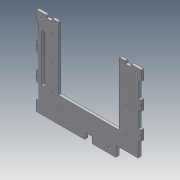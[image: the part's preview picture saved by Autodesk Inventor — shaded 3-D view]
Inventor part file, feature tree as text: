
AUTODESK INVENTOR PART (.ipt)
format: ipt  version: 2014 (Build 180170000, 170)  size: 314,368 bytes
history: native  units: mm
features: extrude x9, sketch x9, fillet x2
ambient origin geometry x8: Origin, YZ Plane, XZ Plane, XY Plane, X Axis, Y Axis, Z Axis, Center Point
bodies: Solid1 (feature_tree)
feature tree (20):
  extrude  "Extrusion1"  Depth=175.0mm
  extrude  "Extrusion2"  Depth=185.0mm
  extrude  "Extrusion3"  Depth=6.0mm TaperAngle=0.0deg
  extrude  "Extrusion4"  Depth=59.0mm
  extrude  "Extrusion5"  Depth=6.0mm TaperAngle=0.0deg
  extrude  "Extrusion6"  Depth=8.0mm
  extrude  "Extrusion7"  Depth=108.0mm
  extrude  "Extrusion8"  Depth=60.0mm
  extrude  "Extrusion9"  Depth=175.0mm
  fillet  "Fillet1"  Radius=3.2mm
  fillet  "Fillet2"  Radius=150.0mm
  sketch  "Sketch1"  dims[d0=175.0mm d1=87.5mm]
  sketch  "Sketch2"  dims[d2=145.0mm d4=185.0mm]
  sketch  "Sketch3"  dims[d5=250.0mm d6=6.0mm d7=0.0mm]
  sketch  "Sketch4"  dims[d8=3.0mm d9=0.0mm d10=59.0mm]
  sketch  "Sketch5"  dims[d11=25.0mm d13=6.0mm d14=0.0mm]
  sketch  "Sketch6"  dims[d15=35.0mm d16=8.0mm]
  sketch  "Sketch7"  dims[d17=108.0mm d18=40.0mm]
  sketch  "Sketch8"  dims[d19=10.0mm d20=0.0mm d21=60.0mm]
  sketch  "Sketch9"  dims[d22=60.0mm d23=175.0mm d24=3.2mm d25=150.0mm d26=15.0mm d27=10.0mm d28=0.0mm d29=50.0mm d30=54.0mm d31=3.0mm d32=4.4mm d33=30.0mm d34=15.0mm d35=10.0mm d36=0.0mm d37=2.0mm d38=16.0mm d39=15.0mm d40=10.0mm d41=0.0mm d42=12.5mm d43=50.0mm d44=50.0mm d45=5.4mm d46=12.5mm d47=12.5mm d48=12.5mm d49=5.4mm d50=25.0mm d51=6.1mm d52=25.0mm d53=25.0mm d54=2.2mm d55=12.5mm d56=12.5mm d57=10.0mm d58=0.0mm d59=2.0mm d60=12.5mm d63=10.0mm d64=0.0mm d66=25.0mm d68=8.0mm d69=8.0mm d70=25.0mm]
